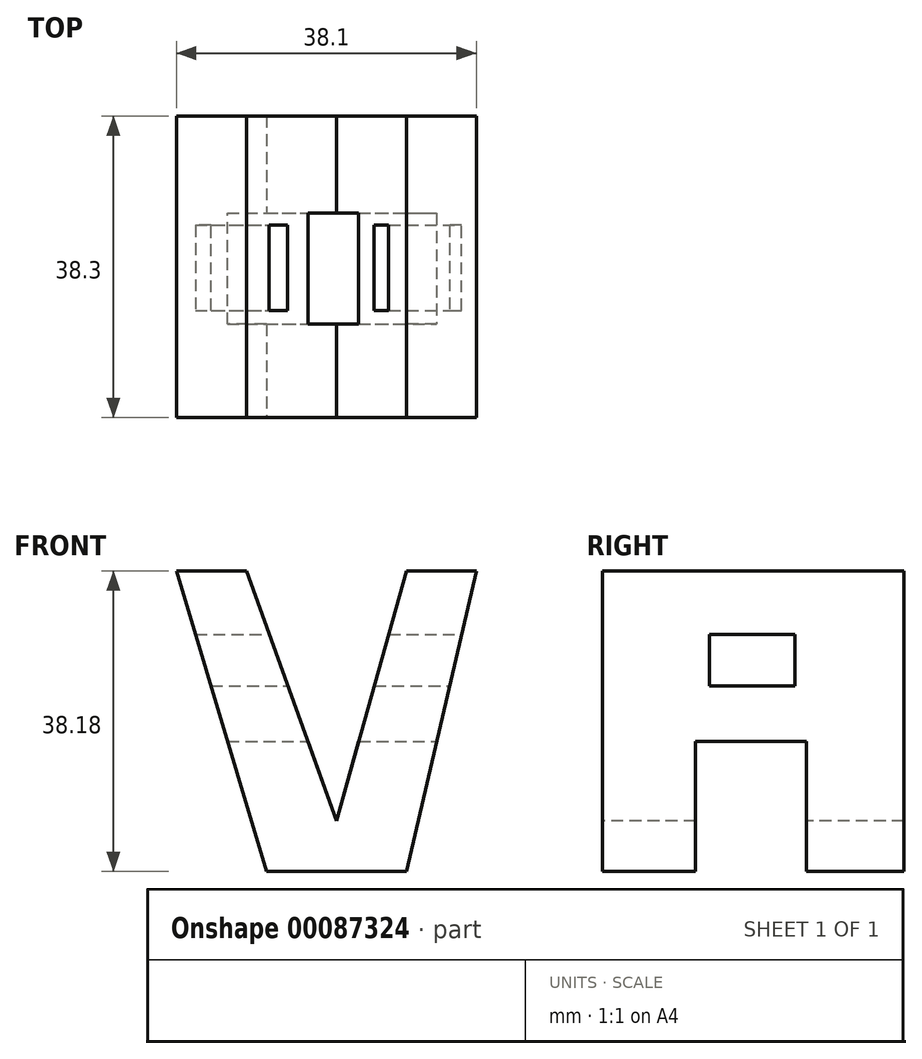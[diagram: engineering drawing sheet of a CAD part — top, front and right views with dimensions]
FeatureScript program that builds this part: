
annotation { "Feature Type Name" : "Feature", "Feature Type Description" : "" }
export const myFeature = defineFeature(function(context is Context, id is Id, definition is map)
    precondition{}
    {
        {
            var Q0;
            Q0=qCreatedBy(makeId("Right.planeOp"),FACE);
            var sketch = newSketch(context, id + "F0", { "sketchPlane" : qUnion([Q0])});
            skLineSegment(sketch, "E0", {"start": v(0, 0) * mm, "end": v(38.3, 0) * mm});
            skLineSegment(sketch, "E1", {"start": v(38.3, 0) * mm, "end": v(38.3, 38.18) * mm});
            skLineSegment(sketch, "E2", {"start": v(38.3, 38.18) * mm, "end": v(0, 38.18) * mm});
            skLineSegment(sketch, "E3", {"start": v(0, 38.18) * mm, "end": v(0, 0) * mm});
            skSolve(sketch);
        }
        {
            var Q0;
            Q0=makeQuery(id+"F0.imprint","IMPRINT",FACE,{"disambiguationData":[TD([[makeQuery(id+"F0.imprint","IMPRINT",EDGE,{"derivedFrom":sQuery(id+"F0.wireOp",EDGE,"E0")}),1.0]])]});
            extrude(context, id + "F1", {"entities" : qUnion([Q0]), "oppositeDirection" : true, "depth" : 38.1 * mm});
        }
        {
            var Q0;
            Q0=qCreatedBy(makeId("Right.planeOp"),FACE);
            var sketch = newSketch(context, id + "F2", { "sketchPlane" : qUnion([Q0])});
            skLineSegment(sketch, "E4", {"start": v(0, 0) * mm, "end": v(0, 38.1) * mm});
            skLineSegment(sketch, "E5", {"start": v(0, 38.1) * mm, "end": v(38.1, 38.1) * mm});
            skLineSegment(sketch, "E6", {"start": v(38.1, 38.1) * mm, "end": v(38.1, 0) * mm});
            skLineSegment(sketch, "E7", {"start": v(38.1, 0) * mm, "end": v(0, 0) * mm});
            skLineSegment(sketch, "E8", {"start": v(11.84, 0) * mm, "end": v(11.84, 16.5) * mm});
            skLineSegment(sketch, "E9", {"start": v(11.84, 16.5) * mm, "end": v(25.96, 16.5) * mm});
            skLineSegment(sketch, "E10", {"start": v(25.96, 16.5) * mm, "end": v(25.96, 0) * mm});
            skLineSegment(sketch, "E11", {"start": v(13.6, 30.11) * mm, "end": v(13.6, 23.56) * mm});
            skLineSegment(sketch, "E12", {"start": v(13.6, 23.56) * mm, "end": v(24.44, 23.56) * mm});
            skLineSegment(sketch, "E13", {"start": v(24.44, 23.56) * mm, "end": v(24.44, 30.11) * mm});
            skLineSegment(sketch, "E14", {"start": v(24.44, 30.11) * mm, "end": v(13.6, 30.11) * mm});
            skSolve(sketch);
        }
        {
            var Q0;
            Q0=makeQuery(id+"F2.imprint","IMPRINT",FACE,{"disambiguationData":[TD([[makeQuery(id+"F2.imprint","IMPRINT",EDGE,{"derivedFrom":sQuery(id+"F2.wireOp",EDGE,"E11")}),1.0]])]});
            var Q1;
            {var subQ0=sQuery(id+"F2.wireOp",EDGE,"E8");Q1=makeQuery(id+"F2.imprint","IMPRINT",FACE,{"disambiguationData":[TD([[makeQuery(id+"F2.imprint","IMPRINT",EDGE,{"derivedFrom":subQ0}),-1.0]])]});}
            extrude(context, id + "F3", {"entities" : qUnion([Q0, Q1]), "operationType" : NewBodyOperationType.REMOVE, "oppositeDirection" : true, "depth" : 38.1 * mm});
        }
        {
            var Q0;
            Q0=makeQuery(id+"F1.opExtrude","SWEPT_FACE",FACE,{"disambiguationData":[OSD([sQuery(id+"F0.wireOp",EDGE,"E3")])]});
            var sketch = newSketch(context, id + "F4", { "sketchPlane" : qUnion([Q0])});
            skLineSegment(sketch, "E15", {"start": v(0, 0) * mm, "end": v(-38.1, 0) * mm});
            skLineSegment(sketch, "E16", {"start": v(-38.1, 0) * mm, "end": v(-38.1, 38.18) * mm});
            skLineSegment(sketch, "E17", {"start": v(-38.1, 38.18) * mm, "end": v(0, 38.18) * mm});
            skLineSegment(sketch, "E18", {"start": v(0, 38.18) * mm, "end": v(0, 0) * mm});
            skLineSegment(sketch, "E19", {"start": v(-38.1, 38.18) * mm, "end": v(-26.67, 0) * mm});
            skLineSegment(sketch, "E20", {"start": v(-26.67, 0) * mm, "end": v(-8.89, 0) * mm});
            skLineSegment(sketch, "E21", {"start": v(-8.9, 0) * mm, "end": v(0, 38.18) * mm});
            skLineSegment(sketch, "E22", {"start": v(-8.89, 38.18) * mm, "end": v(-17.78, 6.43) * mm});
            skLineSegment(sketch, "E23", {"start": v(-17.78, 6.43) * mm, "end": v(-29.21, 38.18) * mm});
            skSolve(sketch);
        }
        {
            var Q0;
            {var subQ0=sQuery(id+"F4.wireOp",EDGE,"E22");Q0=makeQuery(id+"F4.imprint","IMPRINT",FACE,{"disambiguationData":[TD([[makeQuery(id+"F4.imprint","IMPRINT",EDGE,{"derivedFrom":subQ0}),-1.0]])]});}
            var Q1;
            {var subQ0=sQuery(id+"F4.wireOp",EDGE,"E16");Q1=makeQuery(id+"F4.imprint","IMPRINT",FACE,{"disambiguationData":[TD([[makeQuery(id+"F4.imprint","IMPRINT",EDGE,{"derivedFrom":subQ0}),1.0]])]});}
            var Q2;
            {var subQ0=sQuery(id+"F4.wireOp",EDGE,"E18");Q2=makeQuery(id+"F4.imprint","IMPRINT",FACE,{"disambiguationData":[TD([[makeQuery(id+"F4.imprint","IMPRINT",EDGE,{"derivedFrom":subQ0}),-1.0]])]});}
            extrude(context, id + "F5", {"entities" : qUnion([Q0, Q1, Q2]), "operationType" : NewBodyOperationType.REMOVE, "oppositeDirection" : true, "depth" : 38.1 * mm});
        }
        {
            var Q0;
            Q0=makeQuery(id+"F5.boolean.opBoolean","COPY",FACE,{"derivedFrom":makeQuery(id+"F5.opExtrude","CAP_FACE",FACE,{"disambiguationData":[OSD([sQuery(id+"F4.wireOp",EDGE,"E17"),sQuery(id+"F4.wireOp",EDGE,"E22"),sQuery(id+"F4.wireOp",EDGE,"E23")])],"isStart":false})});
            var Q1;
            Q1=makeQuery(id+"F5.boolean.opBoolean","COPY",FACE,{"derivedFrom":makeQuery(id+"F5.opExtrude","CAP_FACE",FACE,{"disambiguationData":[OSD([sQuery(id+"F4.wireOp",EDGE,"E15"),sQuery(id+"F4.wireOp",EDGE,"E16"),sQuery(id+"F4.wireOp",EDGE,"E19")])],"isStart":false})});
            var Q2;
            Q2=makeQuery(id+"F5.boolean.opBoolean","COPY",FACE,{"derivedFrom":makeQuery(id+"F5.opExtrude","CAP_FACE",FACE,{"disambiguationData":[OSD([sQuery(id+"F4.wireOp",EDGE,"E15"),sQuery(id+"F4.wireOp",EDGE,"E18"),sQuery(id+"F4.wireOp",EDGE,"E21")])],"isStart":false})});
            extrude(context, id + "F6", {"entities" : qUnion([Q0, Q1, Q2]), "operationType" : NewBodyOperationType.REMOVE, "oppositeDirection" : true, "depth" : 25.4 * mm});
        }
        {
            var Q0;
            {var subQ1=sQuery(id+"F4.wireOp",EDGE,"E21");Q0=makeQuery(id+"F6.boolean.opBoolean","SPLIT",FACE,{"disambiguationData":[TD([makeQuery(id+"F5.boolean.opBoolean","COPY",FACE,{"derivedFrom":makeQuery(id+"F5.opExtrude","SWEPT_FACE",FACE,{"disambiguationData":[OSD([subQ1])]})})])],"derivedFrom":makeQuery(id+"F1.opExtrude","SWEPT_FACE",FACE,{"disambiguationData":[OSD([sQuery(id+"F0.wireOp",EDGE,"E2")])]})});}
            var Q1;
            {var subQ1=sQuery(id+"F4.wireOp",EDGE,"E19");Q1=makeQuery(id+"F6.boolean.opBoolean","SPLIT",FACE,{"disambiguationData":[TD([makeQuery(id+"F5.boolean.opBoolean","COPY",FACE,{"derivedFrom":makeQuery(id+"F5.opExtrude","SWEPT_FACE",FACE,{"disambiguationData":[OSD([subQ1])]})})])],"derivedFrom":makeQuery(id+"F1.opExtrude","SWEPT_FACE",FACE,{"disambiguationData":[OSD([sQuery(id+"F0.wireOp",EDGE,"E2")])]})});}
            extrude(context, id + "F7", {"entities" : qUnion([Q0, Q1]), "operationType" : NewBodyOperationType.REMOVE, "depth" : 25.4 * mm});
        }
    });
